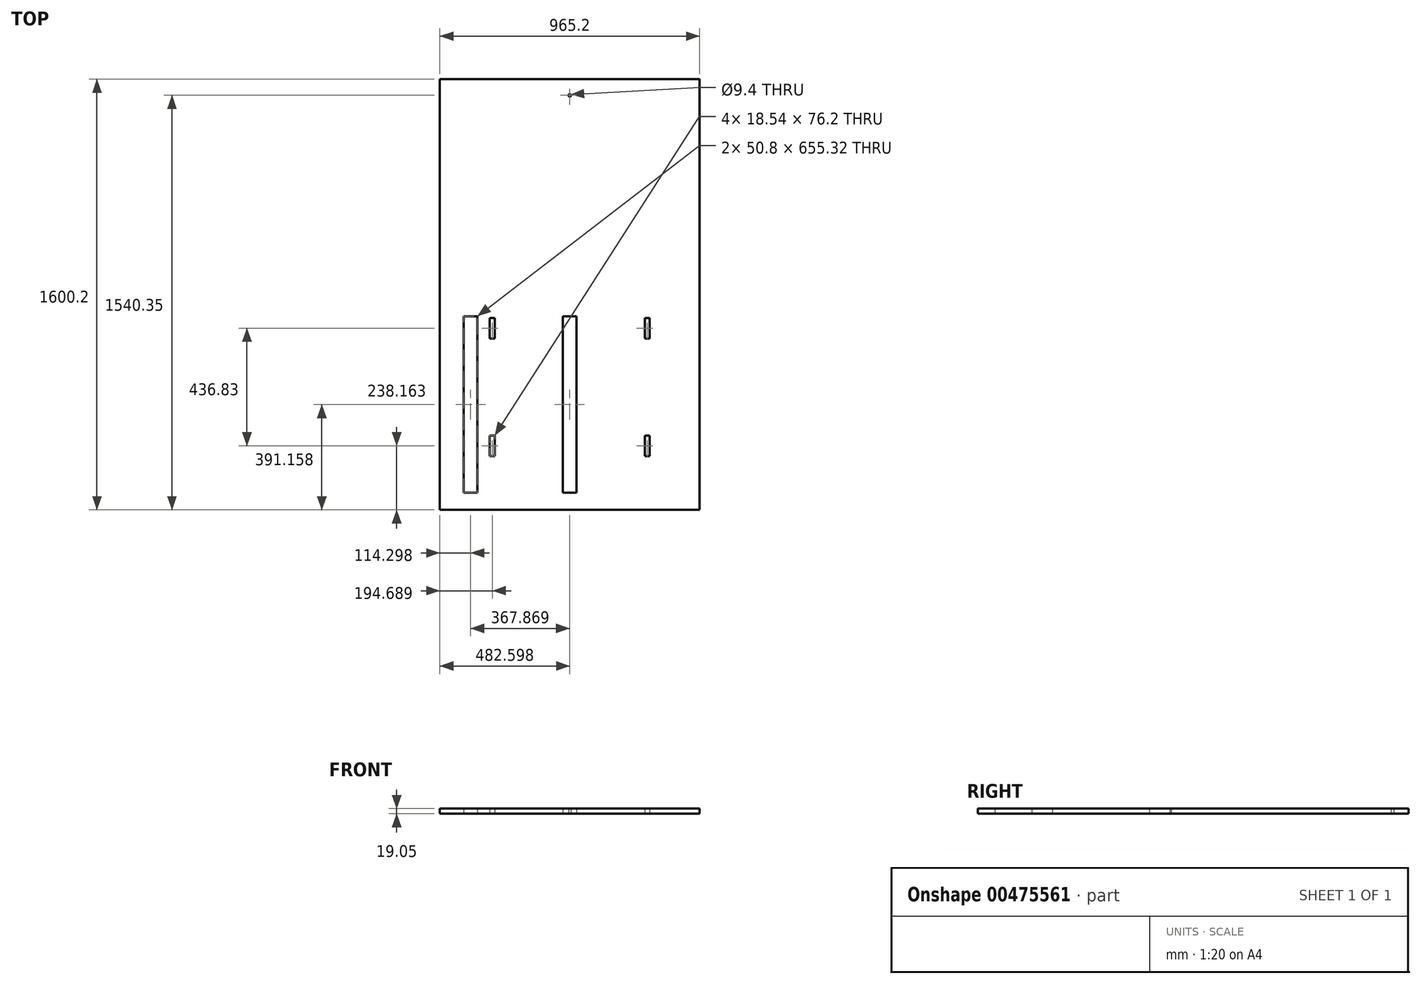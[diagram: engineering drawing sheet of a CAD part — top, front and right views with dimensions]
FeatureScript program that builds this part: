
annotation { "Feature Type Name" : "Feature", "Feature Type Description" : "" }
export const myFeature = defineFeature(function(context is Context, id is Id, definition is map)
    precondition{}
    {
        {
            var Q0;
            Q0=qCreatedBy(makeId("Top.planeOp"),FACE);
            var sketch = newSketch(context, id + "F0", { "sketchPlane" : qUnion([Q0])});
            skLineSegment(sketch, "E0.bottom", {"start": v(-436.38, 820.74) * mm, "end": v(1163.82, 820.74) * mm});
            skLineSegment(sketch, "E0.top", {"start": v(-436.38, -144.46) * mm, "end": v(1163.82, -144.46) * mm});
            skLineSegment(sketch, "E0.left", {"start": v(-436.38, 820.74) * mm, "end": v(-436.38, -144.46) * mm});
            skLineSegment(sketch, "E0.right", {"start": v(1163.82, 820.74) * mm, "end": v(1163.82, -144.46) * mm});
            skLineSegment(sketch, "E1.bottom", {"start": v(1100.32, -55.56) * mm, "end": v(445, -55.56) * mm});
            skLineSegment(sketch, "E1.top", {"start": v(1100.32, -4.76) * mm, "end": v(445, -4.76) * mm});
            skLineSegment(sketch, "E1.left", {"start": v(1100.32, -55.56) * mm, "end": v(1100.32, -4.76) * mm});
            skLineSegment(sketch, "E1.right", {"start": v(445, -55.56) * mm, "end": v(445, -4.76) * mm});
            skLineSegment(sketch, "E2.bottom", {"start": v(1100.32, 312.3) * mm, "end": v(445, 312.3) * mm});
            skLineSegment(sketch, "E2.top", {"start": v(1100.32, 363.1) * mm, "end": v(445, 363.1) * mm});
            skLineSegment(sketch, "E2.left", {"start": v(1100.32, 312.3) * mm, "end": v(1100.32, 363.1) * mm});
            skLineSegment(sketch, "E2.right", {"start": v(445, 312.3) * mm, "end": v(445, 363.1) * mm});
            skLineSegment(sketch, "E3.bottom", {"start": v(450.72, 635.32) * mm, "end": v(526.92, 635.32) * mm});
            skLineSegment(sketch, "E3.top", {"start": v(450.72, 616.78) * mm, "end": v(526.92, 616.78) * mm});
            skLineSegment(sketch, "E3.left", {"start": v(450.72, 635.32) * mm, "end": v(450.72, 616.78) * mm});
            skLineSegment(sketch, "E3.right", {"start": v(526.92, 635.32) * mm, "end": v(526.92, 616.78) * mm});
            skLineSegment(sketch, "E4.bottom", {"start": v(450.72, 59.5) * mm, "end": v(526.92, 59.5) * mm});
            skLineSegment(sketch, "E4.top", {"start": v(450.72, 40.96) * mm, "end": v(526.92, 40.96) * mm});
            skLineSegment(sketch, "E4.left", {"start": v(450.72, 59.5) * mm, "end": v(450.72, 40.96) * mm});
            skLineSegment(sketch, "E4.right", {"start": v(526.92, 59.5) * mm, "end": v(526.92, 40.96) * mm});
            skLineSegment(sketch, "E5.bottom", {"start": v(887.55, 635.32) * mm, "end": v(963.75, 635.32) * mm});
            skLineSegment(sketch, "E5.top", {"start": v(887.55, 616.78) * mm, "end": v(963.75, 616.78) * mm});
            skLineSegment(sketch, "E5.left", {"start": v(887.55, 635.32) * mm, "end": v(887.55, 616.78) * mm});
            skLineSegment(sketch, "E5.right", {"start": v(963.75, 635.32) * mm, "end": v(963.75, 616.78) * mm});
            skLineSegment(sketch, "E6.bottom", {"start": v(887.55, 59.5) * mm, "end": v(963.75, 59.5) * mm});
            skLineSegment(sketch, "E6.top", {"start": v(887.55, 40.96) * mm, "end": v(963.75, 40.96) * mm});
            skLineSegment(sketch, "E6.left", {"start": v(887.55, 59.5) * mm, "end": v(887.55, 40.96) * mm});
            skLineSegment(sketch, "E6.right", {"start": v(963.75, 59.5) * mm, "end": v(963.75, 40.96) * mm});
            skCircle(sketch, "E7", {"center": v(-376.53, 338.14) * mm, "radius": 4.7 * mm});
            skPoint(sketch, "E7.centerSnap0", {"position": v(-436.38, 338.14) * mm});
            skSolve(sketch);
        }
        {
            var Q0;
            Q0 = qSketchRegion(id + "F0", true);
            extrude(context, id + "F1", {"entities" : qUnion([Q0]), "depth" : 19.05 * mm});
        }
        {
            var Q0;
            Q0=makeQuery(id+"F1.opExtrude","SWEPT_BODY",BODY,{"disambiguationData":[OSD([sQuery(id+"F0.wireOp",EDGE,"E0.bottom"),sQuery(id+"F0.wireOp",EDGE,"E0.top"),sQuery(id+"F0.wireOp",EDGE,"E0.left"),sQuery(id+"F0.wireOp",EDGE,"E0.right")])]});
            var Q1;
            Q1=makeQuery(id+"F1.opExtrude","SWEPT_EDGE",EDGE,{"disambiguationData":[OSD([sQuery(id+"F0.wireOp",EDGE,"E0.top"),sQuery(id+"F0.wireOp",EDGE,"E0.left")])]});
            transform(context, id + "F2", {"entities" : qUnion([Q0]), "transformType" : TransformType.ROTATION, "transformAxis" : qUnion([Q1]), "angle" : 90 * degree, "makeCopy" : false});
        }
    });
